# Revit family: Merida Dozownik mydła w płynie STELLA MINI pojemność 400 ml
name_source: partatom
category: Modele ogólne
revit_build: Autodesk Revit 2015 (Build: 20140606_1530(x64)
units: mm (PartAtom-declared; Revit-internal decimal feet)

## types (3) — shared parameters
Autor = www.archispace.pl
Domyślna rzędna = 900 mm  [stored 2.95276 ft]
Głębokość = 87 mm  [stored 0.285433 ft]
Karta techniczna produktu = https://sklep.merida.com.pl
Pojemność = 0,4l
Producent = MERIDA SP. Z O.O.
Rodzaj montażu = ścienny
Sposób dozowania = dozowanie ręczne
Strona produktu = https://sklep.merida.com.pl
Szerokość = 98 mm  [stored 0.321522 ft]
Typ mydła = mydło w płynie
URL = www.merida.com.pl
Wielkość = MINI
Wysokość = 190 mm

## per-type parameters (varying)
| type | Kolor | Linia | Materiał obudowa | Materiał obudowy | Model | Opis |
| DSM102 | matowa | MERIDA STELLA | Merida_Stal_Matowa | stal nierdzewna | Dozownik mydła w płynie Merida Stella Mini, matowy | DSM102, dozownik mydła w płynie, stal nierdzewna matowa, montaż naścienny, łączenia boków spawane i szlifowane, niewidoczne zawiasy, metalowy zamek bębenkowy licowany z powierzchnią urządzenia, okienko kontroli poziomu mydła, zbiornik na mydło z tworzywa sztucznego, możliwość wyjęcia zbiornika ułatwia okresowe czyszczenie, mydło uzupełniane z kanistra |
| DSP102 | polerowana | MERIDA STELLA | Merida_Stal_Polerowana | stal nierdzewna | Dozownik mydła w płynie Merida Stella Mini polerowany | DSP102, dozownik mydła w płynie, stal nierdzewna polerowana, montaż naścienny, łączenia boków spawane i polerowane, niewidoczne zawiasy, metalowy zamek bębenkowy licowany z powierzchnią urządzenia, okienko kontroli poziomu mydła, zbiornik na mydło z tworzywa sztucznego, możliwość wyjęcia zbiornika ułatwia okresowe czyszczenie, mydło uzupełnia się z kanistra |
| DSB102 | biały | MERIDA STELLA BIAŁA | Merida_biały_półmat | stal nierdzewna malowana proszkowo | Dozownik mydła w płynie Merida Stella Mini, biały | DSB102, dozownik mydła w płynie, stal malowana proszkowo na biało, montaż naścienny, łączenia boków spawane, niewidoczne zawiasy, metalowy zamek bębenkowy licowany z powierzchnią urządzenia, okienko kontroli poziomu mydła, zbiornik na mydło z tworzywa sztucznego, możliwość wyjęcia zbiornika ułatwia okresowe czyszczenie, mydło uzupełniane z kanistra |

note: column(s) folded — value = type name in every type: Numer katalogowy

note: [stored X ft] marks values corroborated as IEEE doubles in the binary element streams (Revit-internal decimal feet)
